# Revit family: _Шведская стенка+разноуровневые турники+брусья+рукоход зигзаг+скамья для пресса+канат 2
name_source: partatom
category: Антураж
revit_build: Autodesk Revit 2018 (Build: 20170927_1515(x64)
units: mm (PartAtom-declared; Revit-internal decimal feet)

## family parameters
Всегда вертикально = Да
Источник визуального образа = Геометрия семейства
На основе рабочей плоскости = Нет
Общий = Нет
При загрузке вырезать с полостями = Нет
Точка расчета площади = Нет

## types (1)
- Воркаут ЭКО-23 «Шведская стенка + разноуровневые турники + брусья + рукоход зигзаг + скамья для пресса + канат»
    URL = https://hobbyka.ru
    Артикул товара = Арт. 43435
    Высота = 2850 мм
    Группа модели = Спортивные площадки в ЭКО-стиле
    Длина = 6500 мм
    Изготовитель = ООО «Хоббика»
    Изображение типоразмера = Шведская стенка+разноуровневые турники+брусья+рукоход зигзаг+скамья для пресса+канат (2) 001.png
    Материал изделия = Дерево, , нержавеющая сталь
    Описание = Воркаут ЭКО-23 «Шведская стенка + разноуровневые турники + брусья + рукоход зигзаг + скамья для пресса + канат»
    Цвет каркаса = Орегон
    Ширина = 2300 мм
